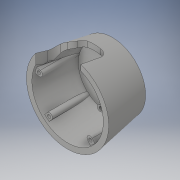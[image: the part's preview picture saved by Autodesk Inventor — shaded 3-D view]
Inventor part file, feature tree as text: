
AUTODESK INVENTOR PART (.ipt)
format: ipt  version: 2018 (Build 220112000, 112)  size: 261,120 bytes
history: native  units: in
note: dims shown in document units (in); Inventor stores cm internally (conversion verified against a paired STEP export)
features: extrude x5, sketch x2, shell x1, fillet x1, plane x1, hole x1
ambient origin geometry x8: Origin, YZ Plane, XZ Plane, XY Plane, X Axis, Y Axis, Z Axis, Center Point
bodies: Solid1 (feature_tree)
feature tree (11):
  sketch  "Sketch1"  dims[d0=1.9685in d1=1.1811in d2=0.1969in]
  extrude  "Extrusion1"  Depth=1.1811in
  shell  "Shell1"  Thickness=0.1969in
  extrude  "Extrusion2"  Depth=0.3937in
  sketch  "Sketch2"  dims[d3=0.7874in d5=360.0deg d8=0.315in d9=0.1969in d10=1.3268in d11=0.0687in d12=0.1575in d13=2.9528in d14=0.0in d18=0.1064in d19=0.1054in d20=0.3406in d21=0.3392in d22=0.9323in d23=0.9324in d24=0.918in d25=0.9259in d26=0.1772in d27=0.1772in d28=0.1772in d29=0.1772in d32=0.0886in d33=0.0886in d34=0.0886in d35=0.0886in d36=0.0886in d37=0.0886in d40=0.0197in d41=0.0197in d42=0.0197in d43=0.0197in d44=0.0984in d45=0.2362in d46=0.1575in d47=0.0787in d48=90.0deg d49=0.4724in d50=0.0in d51=0.3937in d52=0.3937in d53=0.5512in d54=0.7874in d55=0.0in d56=0.5512in d57=0.0in d58=0.1969in d59=-0.0669in d60=0.3937in d61=0.0in]
  extrude  "Extrusion4"  Depth=0.3937in
  extrude  "Extrusion5"  Depth=0.3937in
  fillet  "Fillet1"  Radius=0.1575in
  plane  "Work Plane1"
  extrude  "Extrusion6"  Depth=0.3937in TaperAngle=0.0deg
  hole  "Hole1"  [1 undecoded]
note: 1 required parameter value undecoded (feature->parameter linkage not recoverable at this tier; creation-order binding heuristic only, values carry confidence <= 0.55)
